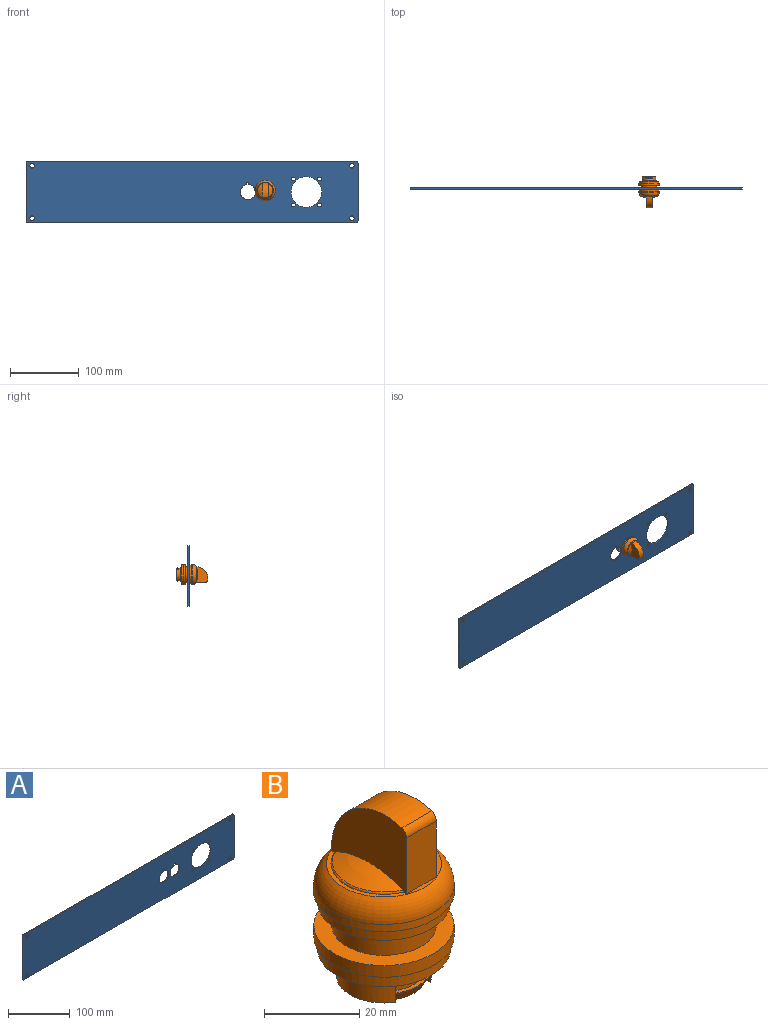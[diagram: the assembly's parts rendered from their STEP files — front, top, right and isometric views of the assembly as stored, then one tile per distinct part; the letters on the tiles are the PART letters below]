
ASSEMBLY  parts=2 mates=1
PART A: 27 faces, bbox 482.6x2x88 mm
  f0: plane 478.6x2mm, normal (0,0,-1), area 957.2mm2, adj f21,f22,f23,f26
  f1: plane 84x2mm, normal (1,0,0), area 168mm2, adj f21,f22,f23,f24
  f2: plane 478.6x2mm, normal (0,0,1), area 957.2mm2, adj f21,f22,f24,f25
  f3: plane 3x2mm, normal (0,0,-1), area 6mm2, adj f4,f10,f21,f22
  f4: plane 3.1x2mm, normal (-1,0,0), area 6.2mm2, adj f3,f5,f21,f22
  f5: cylinder r=11.1mm len=22.2mm, axis (0,1,0), area 133.5mm2, adj f4,f10,f21,f22
  f6: plane 3x2mm, normal (0,0,-1), area 6mm2, adj f7,f11,f21,f22
  f7: plane 3.1x2mm, normal (-1,0,0), area 6.2mm2, adj f6,f8,f21,f22
  f8: cylinder r=11.1mm len=22.2mm, axis (0,1,0), area 133.5mm2, adj f7,f11,f21,f22
  f9: plane 84x2mm, normal (-1,0,0), area 168mm2, adj f21,f22,f25,f26
  f10: plane 3.1x2mm, normal (1,0,0), area 6.2mm2, adj f3,f5,f21,f22
  f11: plane 3.1x2mm, normal (1,0,0), area 6.2mm2, adj f6,f8,f21,f22
  f12: cylinder r=3.25mm len=6.5mm, axis (0,1,0), area 40.8mm2, adj f21,f22
  f13: cylinder r=3.25mm len=6.5mm, axis (0,1,0), area 40.8mm2, adj f21,f22
  f14: cylinder r=3.25mm len=6.5mm, axis (0,1,0), area 40.8mm2, adj f21,f22
  f15: cylinder r=22.25mm len=44.5mm, axis (0,1,0), area 279.6mm2, adj f21,f22
  f16: cylinder r=2.75mm len=5.5mm, axis (0,1,0), area 34.6mm2, adj f21,f22
  f17: cylinder r=2.75mm len=5.5mm, axis (0,1,0), area 34.6mm2, adj f21,f22
  f18: cylinder r=2.75mm len=5.5mm, axis (0,1,0), area 34.6mm2, adj f21,f22
  f19: cylinder r=2.75mm len=5.5mm, axis (0,1,0), area 34.6mm2, adj f21,f22
  f20: cylinder r=3.25mm len=6.5mm, axis (0,1,0), area 40.8mm2, adj f21,f22
  f21: plane 482.6x88mm, normal (0,-1,0), area 39890mm2, adj f0,f1,f2,f3,f4,f5,f6,f7
  f22: plane 482.6x88mm, normal (0,1,0), area 39890mm2, adj f0,f1,f2,f3,f4,f5,f6,f7
  f23: cylinder r=2mm len=2mm, axis (0,1,0), area 6.3mm2, adj f0,f1,f21,f22
  f24: cylinder r=2mm len=2mm, axis (0,-1,0), area 6.3mm2, adj f1,f2,f21,f22
  f25: cylinder r=2mm len=2mm, axis (0,1,0), area 6.3mm2, adj f2,f9,f21,f22
  f26: cylinder r=2mm len=2mm, axis (0,-1,0), area 6.3mm2, adj f0,f9,f21,f22
PART B: 49 faces, bbox 32.1x32.1x46 mm
  f0: sphere r=25mm, area 98.3mm2, adj f1,f36
  f1: torus R=10.65mm, axis (0,0,1), area 14mm2, adj f0,f36,f42
  f2: torus R=7.78mm, axis (0,0,1), area 522mm2, adj f3,f42
  f3: cone r=14.81mm half-angle=2.6deg, axis (0,0,-1), area 168.9mm2, adj f2,f48
  f4: cylinder r=14mm len=28mm, axis (0,0,1), area 246.3mm2, adj f47,f48
  f5: cone r=10.54mm half-angle=45deg, axis (0,0,1), area 69.7mm2, adj f43,f46
  f6: cylinder r=14.75mm len=29.5mm, axis (0,0,1), area 278mm2, adj f44,f45
  f7: cylinder r=14mm len=28mm, axis (0,0,1), area 263.9mm2, adj f43,f45
  f8: torus R=10.65mm, axis (0,0,1), area 14mm2, adj f9,f41,f42
  f9: sphere r=25mm, area 98.3mm2, adj f8,f41
  f10: cone r=9.5mm half-angle=24.9deg, axis (0,0,1), area 25.6mm2, adj f15,f26,f30,f33
  f11: cylinder r=9.05mm len=10.2mm, axis (0,0,1), area 15.2mm2, adj f13,f29,f31,f35
  f12: cylinder r=9.05mm len=10.2mm, axis (0,0,1), area 15.2mm2, adj f14,f27,f32,f34
  f13: cone r=9.53mm half-angle=24.9deg, axis (0,0,1), area 24.4mm2, adj f11,f15,f29,f31
  f14: cone r=9.53mm half-angle=24.9deg, axis (0,0,1), area 24.4mm2, adj f12,f15,f27,f32
  f15: cylinder r=10mm len=20mm, axis (0,0,1), area 272.8mm2, adj f10,f13,f14,f16,f25,f26,f27,f28
  f16: cone r=9.5mm half-angle=24.9deg, axis (0,0,1), area 23mm2, adj f15,f22,f23,f25,f28,f33
  f17: cylinder r=11mm len=22mm, axis (0,0,1), area 406.6mm2, adj f18,f19,f21,f44,f47
  f18: plane 2x1.18mm, normal (-1,0,0), area 2.4mm2, adj f17,f19,f20,f47
  f19: plane 4x1.18mm, normal (0,0,-1), area 4.2mm2, adj f17,f18,f20,f21
  f20: plane 4x2mm, normal (0,1,0), area 8mm2, adj f18,f19,f21,f47
  f21: plane 2x1.18mm, normal (1,0,0), area 2.4mm2, adj f17,f19,f20,f47
  f22: plane 9.74x1.55mm, normal (-0.71,0,-0.71), area 19.7mm2, adj f16,f23,f24,f33
  f23: plane 9.74x1.55mm, normal (0.71,0,-0.71), area 19.7mm2, adj f16,f22,f24,f33
  f24: plane 3x1.5mm, normal (0,1,0), area 2.2mm2, adj f22,f23,f33
  f25: plane 2.24x1.28mm, normal (-1,0,0), area 1.3mm2, adj f15,f16,f33
  f26: plane 2.24x1.28mm, normal (-1,0,0), area 1.3mm2, adj f10,f15,f33
  f27: plane 3.53x1.21mm, normal (-1,0,0), area 2.7mm2, adj f12,f14,f15,f34
  f28: plane 2.24x1.28mm, normal (1,0,0), area 1.3mm2, adj f15,f16,f33
  f29: plane 3.53x1.21mm, normal (1,0,0), area 2.7mm2, adj f11,f13,f15,f35
  f30: plane 2.24x1.28mm, normal (1,0,0), area 1.3mm2, adj f10,f15,f33
  f31: plane 3.53x1.21mm, normal (-1,0,0), area 2.7mm2, adj f11,f13,f15,f35
  f32: plane 3.53x1.21mm, normal (1,0,0), area 2.7mm2, adj f12,f14,f15,f34
  f33: plane 20x17.87mm, normal (0,0,-1), area 265.7mm2, adj f10,f15,f16,f22,f23,f24,f25,f26
  f34: plane 10.2x2.52mm, normal (0,0,1), area 10.2mm2, adj f12,f15,f27,f32
  f35: plane 10.2x2.52mm, normal (0,0,1), area 10.2mm2, adj f11,f15,f29,f31
  f36: plane 22.35x17.15mm, normal (1,0,0), area 286.5mm2, adj f0,f1,f37,f38,f39,f40,f42
  f37: cylinder r=2mm len=8.84mm, axis (-1,0,0), area 22.2mm2, adj f36,f38,f40,f41
  f38: plane 14.42x8.84mm, normal (0,-1,0), area 127.5mm2, adj f36,f37,f41,f42
  f39: plane 8.84x1.1mm, normal (0,1,0), area 9.7mm2, adj f36,f40,f41,f42
  f40: cylinder r=16mm len=20.91mm, axis (-1,0,0), area 266.3mm2, adj f36,f37,f39,f41
  f41: plane 22.35x17.15mm, normal (-1,0,0), area 286.5mm2, adj f8,f9,f37,f38,f39,f40,f42
  f42: plane 24.21x24.21mm, normal (0,0,1), area 64.6mm2, adj f1,f2,f8,f36,f38,f39,f41
  f43: plane 28x28mm, normal (0,0,-1), area 247.3mm2, adj f5,f7
  f44: plane 29.5x29.5mm, normal (0,0,1), area 303.4mm2, adj f6,f17
  f45: plane 29.5x29.5mm, normal (0,0,-1), area 67.7mm2, adj f6,f7
  f46: plane 20.16x20.16mm, normal (0,0,-1), area 5mm2, adj f5,f15
  f47: plane 28x28mm, normal (0,0,-1), area 231.4mm2, adj f4,f17,f18,f20,f21
  f48: plane 29.7x29.7mm, normal (0,0,-1), area 77mm2, adj f3,f4
PLACE A t=(-11.64,10.49,25.82)mm
PLACE B rot(axis=(1,0,0),90deg) t=(94.65,28.49,27.92)mm
MATE fastened B.f47 <-> A.f21  axis (0,1,0) through (94.65,9.49,39.92)mm
